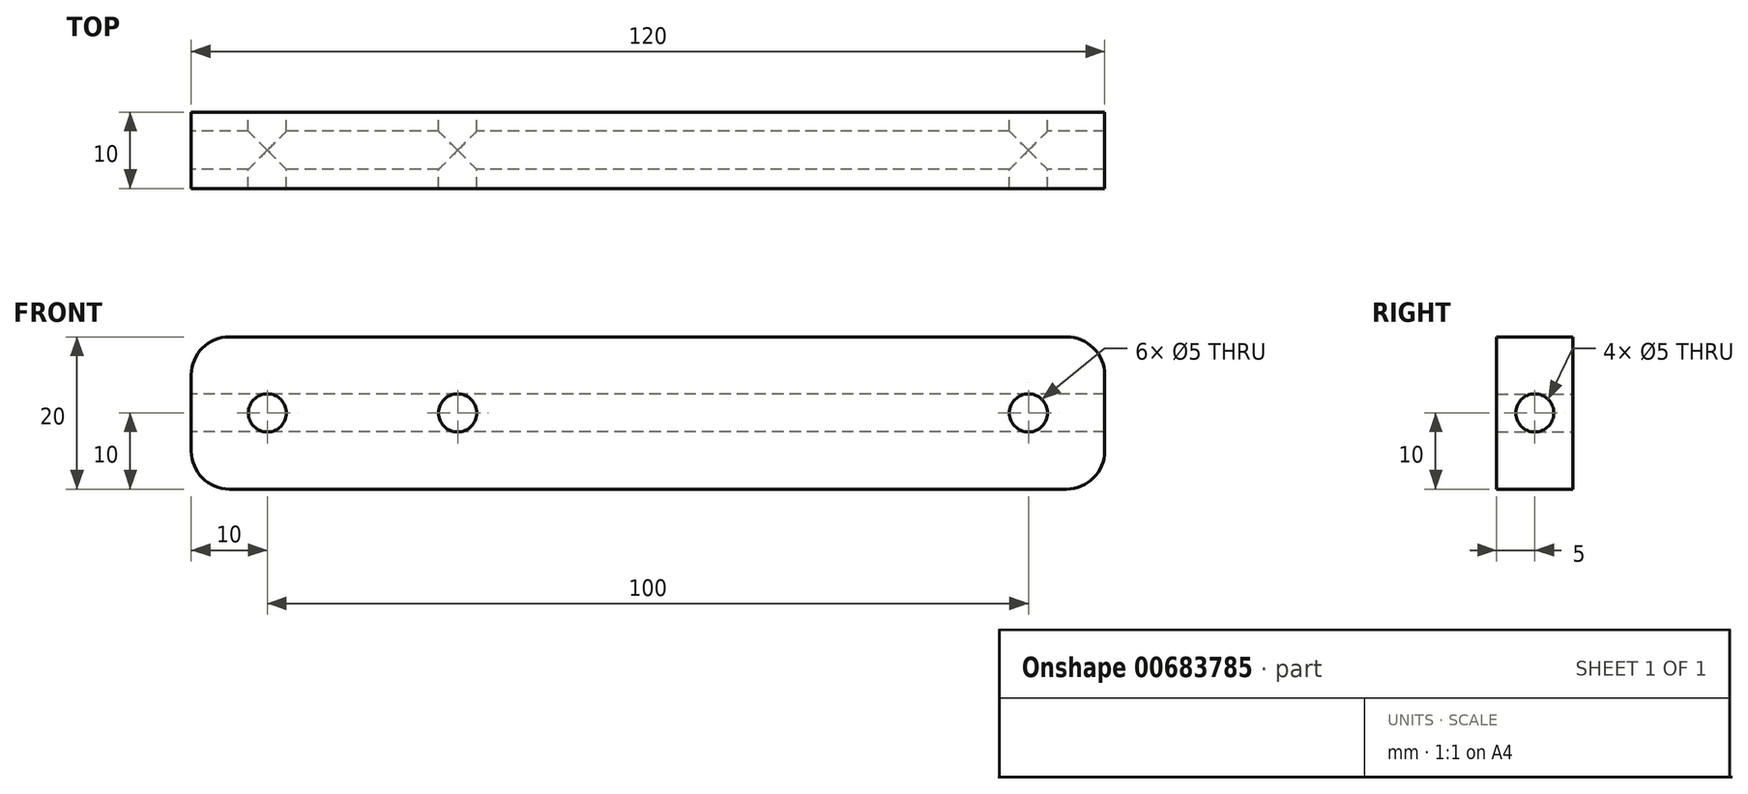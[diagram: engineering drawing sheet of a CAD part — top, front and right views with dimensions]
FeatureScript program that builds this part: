
annotation { "Feature Type Name" : "Feature", "Feature Type Description" : "" }
export const myFeature = defineFeature(function(context is Context, id is Id, definition is map)
    precondition{}
    {
        {
            var Q0;
            Q0=qCreatedBy(makeId("Front.planeOp"),FACE);
            var sketch = newSketch(context, id + "F0", { "sketchPlane" : qUnion([Q0])});
            skLineSegment(sketch, "E0.bottom", {"start": v(55, -10) * mm, "end": v(-55, -10) * mm});
            skLineSegment(sketch, "E0.top", {"start": v(55, 10) * mm, "end": v(-55, 10) * mm});
            skLineSegment(sketch, "E0.left", {"start": v(60, -5) * mm, "end": v(60, 5) * mm});
            skLineSegment(sketch, "E0.right", {"start": v(-60, -5) * mm, "end": v(-60, 5) * mm});
            skPoint(sketch, "E0.middle", {"position": v(0, 0) * mm});
            skLineSegment(sketch, "E1", {"start": v(0, 0) * mm, "end": v(50, 0) * mm});
            skPoint(sketch, "E1.endSnap0", {"position": v(60, 0) * mm});
            skCircle(sketch, "E2", {"center": v(50, 0) * mm, "radius": 2.5 * mm});
            skCircle(sketch, "E3.MirrorC", {"center": v(-50, 0) * mm, "radius": 2.5 * mm});
            skCircle(sketch, "E4", {"center": v(-25, 0) * mm, "radius": 2.5 * mm});
            skPoint(sketch, "E5.visualSharp", {"position": v(-60, -10) * mm});
            skArc(sketch, "E5.filletArc", {"start": v(-60, -5) * mm, "mid": v(-58.54, -8.54) * mm, "end": v(-55, -10) * mm});
            skPoint(sketch, "E6.visualSharp", {"position": v(-60, 10) * mm});
            skArc(sketch, "E6.filletArc", {"start": v(-55, 10) * mm, "mid": v(-58.54, 8.54) * mm, "end": v(-60, 5) * mm});
            skPoint(sketch, "E7.visualSharp", {"position": v(60, -10) * mm});
            skArc(sketch, "E7.filletArc", {"start": v(55, -10) * mm, "mid": v(58.54, -8.54) * mm, "end": v(60, -5) * mm});
            skPoint(sketch, "E8.visualSharp", {"position": v(60, 10) * mm});
            skArc(sketch, "E8.filletArc", {"start": v(60, 5) * mm, "mid": v(58.54, 8.54) * mm, "end": v(55, 10) * mm});
            skSolve(sketch);
        }
        {
            var Q0;
            Q0=makeQuery(id+"F0.imprint","IMPRINT",FACE,{"disambiguationData":[TD([[makeQuery(id+"F0.imprint","IMPRINT",EDGE,{"derivedFrom":sQuery(id+"F0.wireOp",EDGE,"E0.bottom")}),-1.0]])]});
            extrude(context, id + "F1", {"entities" : qUnion([Q0]), "endBound" : BoundingType.SYMMETRIC, "depth" : 10 * mm, "offsetDistance" : 25 * mm});
        }
        {
            var Q0;
            Q0=makeQuery(id+"F1.opExtrude","SWEPT_FACE",FACE,{"disambiguationData":[OSD([sQuery(id+"F0.wireOp",EDGE,"E0.right")])]});
            var sketch = newSketch(context, id + "F2", { "sketchPlane" : qUnion([Q0])});
            skCircle(sketch, "E9", {"center": v(0, 0) * mm, "radius": 2.5 * mm});
            skSolve(sketch);
        }
        {
            var Q0;
            Q0=makeQuery(id+"F2.imprint","IMPRINT",FACE,{"disambiguationData":[TD([[makeQuery(id+"F2.imprint","IMPRINT",EDGE,{"derivedFrom":sQuery(id+"F2.wireOp",EDGE,"E9")}),1.0]])]});
            extrude(context, id + "F3", {"entities" : qUnion([Q0]), "operationType" : NewBodyOperationType.REMOVE, "oppositeDirection" : true, "depth" : 120 * mm, "offsetDistance" : 25 * mm});
        }
    });
